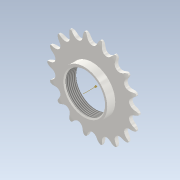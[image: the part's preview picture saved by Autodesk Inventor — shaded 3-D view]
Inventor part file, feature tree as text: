
AUTODESK INVENTOR PART (.ipt)
format: ipt  version: 2021 (Build 250183000, 183)  size: 480,256 bytes
history: native  units: mm
features: other x7, extrude x3, pattern_linear x1, pattern_circular x1, hole x1, chamfer x1, sketch x1
ambient origin geometry x8: Origin, YZ Plane, XZ Plane, XY Plane, X Axis, Y Axis, Z Axis, Center Point
bodies: Solid1 (feature_tree)
feature tree (15):
  other  "Theoretical Tooth Profile"
  other  "Tooth Profile"
  other  "Section Profile"
  other  "Shroud"
  other  "Strand"
  pattern_linear  "Strand Pattern"  Spacing1=3.490659mm  [1 undecoded]
  extrude  "Theoretical Tooth"  Depth=10.0mm
  extrude  "Tooth"  Depth=10.0mm
  pattern_circular  "Tooth Pattern"  [2 undecoded]
  other  "Timing Plane"
  other  "Punto de trabajo1"
  extrude  "Extrusión4"  Depth=10.0mm
  hole  "Agujero1"  [1 undecoded]
  chamfer  "Chaflán1"  Distance=10.85mm
  sketch  "Boceto4"  dims[d0=73.136385mm d2=3.490659mm d3=3.91375mm d10=22.398392mm d11=2.598601mm d12=6.2mm d13=10.11375mm d14=10.85mm d18=10.0mm d19=0.0mm d20=180.0mm d21=360.0deg d23=3.81mm d28=0.0mm d29=0.0mm d30=3.069mm d31=53.102879mm d32=3.069mm d33=0.762mm d34=12.7mm d36=90.0deg d37=90.0deg d38=10.0mm d40=13.92mm d42=0.0mm d43=1.5345mm d44=23.561945mm d45=18.6mm d46=3.91375mm d47=10.0mm d48=0.0mm d49=0.0mm d50=10.0mm d66=10.0mm d67=10.0mm d53=34.376202mm d54=72.0mm d55=66.51mm d56=23.55mm d57=90.0deg d58=8.0mm d59=20.594885mm d60=40.0mm d61=7.0mm d62=0.0mm d63=1.0mm d64=2.0mm d65=45.0deg]
note: 4 required parameter values undecoded (feature->parameter linkage not recoverable at this tier; creation-order binding heuristic only, values carry confidence <= 0.55)
